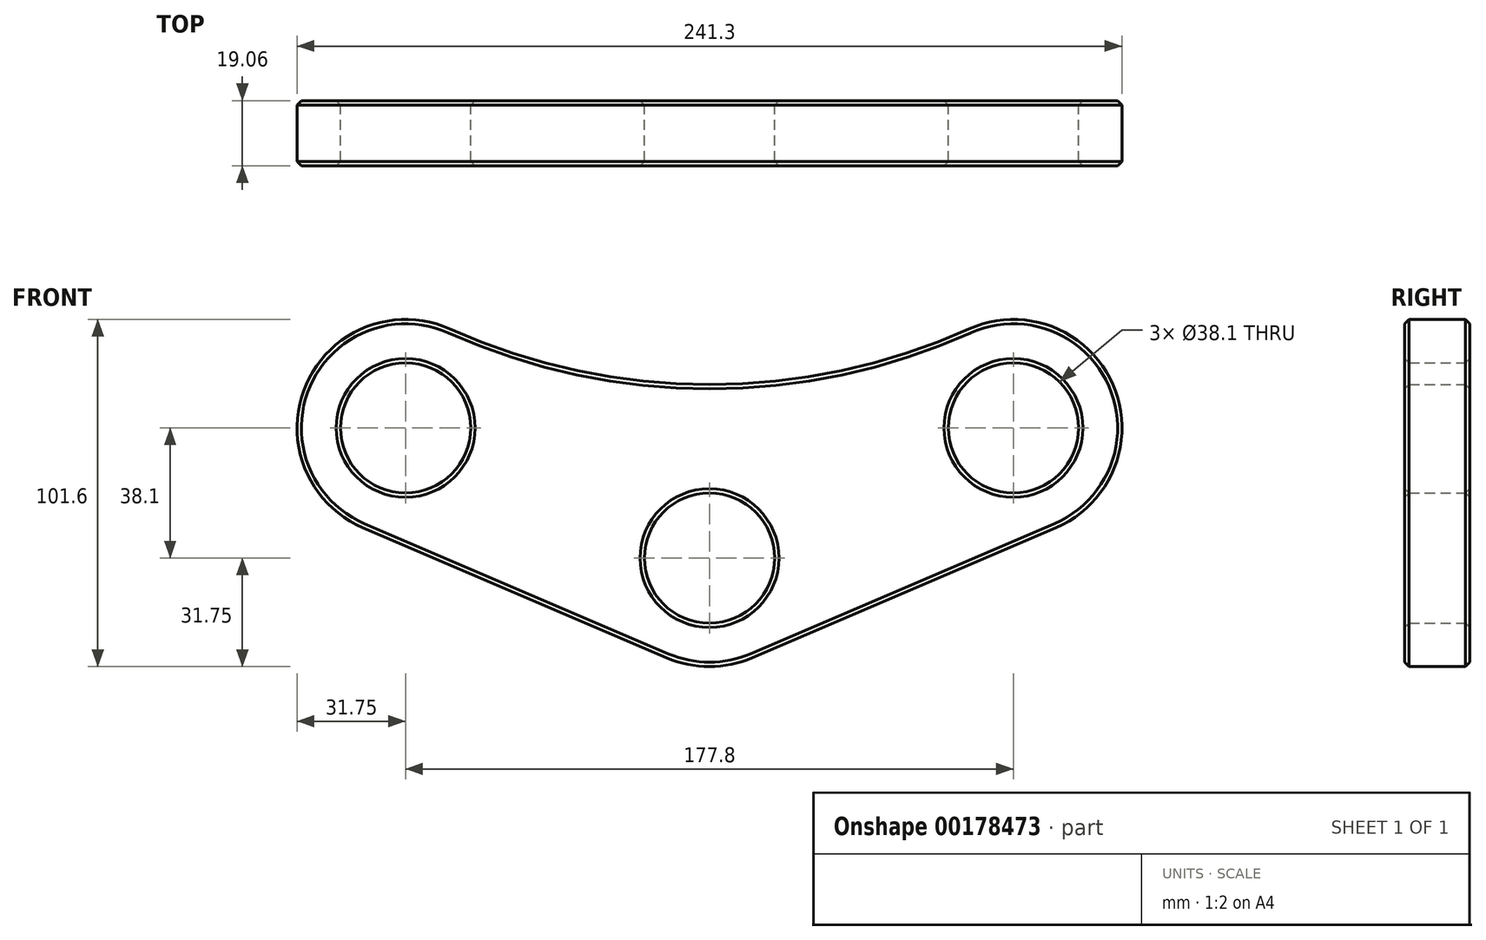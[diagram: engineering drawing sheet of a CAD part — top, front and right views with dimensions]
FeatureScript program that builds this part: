
annotation { "Feature Type Name" : "Feature", "Feature Type Description" : "" }
export const myFeature = defineFeature(function(context is Context, id is Id, definition is map)
    precondition{}
    {
        {
            var Q0;
            Q0=qCreatedBy(makeId("Front.planeOp"),FACE);
            var sketch = newSketch(context, id + "F0", { "sketchPlane" : qUnion([Q0])});
            skArc(sketch, "E0", {"start": v(-12.5, -29.18) * mm, "mid": v(0, -31.75) * mm, "end": v(12.5, -29.18) * mm});
            skArc(sketch, "E1", {"start": v(-75.9, 67.06) * mm, "mid": v(-117.97, 50.86) * mm, "end": v(-101.4, 8.92) * mm});
            skArc(sketch, "E2", {"start": v(101.4, 8.92) * mm, "mid": v(117.97, 50.86) * mm, "end": v(75.9, 67.06) * mm});
            skArc(sketch, "E3", {"start": v(-75.9, 67.06) * mm, "mid": v(0, 50.8) * mm, "end": v(75.9, 67.06) * mm});
            skPoint(sketch, "E3.first.point", {"position": v(-10.84, 113.24) * mm});
            skLineSegment(sketch, "E4", {"start": v(-101.4, 8.92) * mm, "end": v(-12.5, -29.18) * mm});
            skLineSegment(sketch, "E5", {"start": v(12.5, -29.18) * mm, "end": v(101.4, 8.92) * mm});
            skCircle(sketch, "E6", {"center": v(-88.9, 38.1) * mm, "radius": 19.05 * mm});
            skCircle(sketch, "E7", {"center": v(88.9, 38.1) * mm, "radius": 19.05 * mm});
            skCircle(sketch, "E8", {"center": v(0, 0) * mm, "radius": 19.05 * mm});
            skSolve(sketch);
        }
        {
            var Q0;
            Q0 = qSketchRegion(id + "F0", true);
            var Q1;
            Q1=makeQuery(id+"F0.imprint","IMPRINT",FACE,{"disambiguationData":[TD([[makeQuery(id+"F0.imprint","IMPRINT",EDGE,{"derivedFrom":sQuery(id+"F0.wireOp",EDGE,"2Mr1e5ev-CAVB-otBg-7zJ2-05PPhVzjL0mu")}),1.0]])]});
            extrude(context, id + "F1", {"entities" : qUnion([Q0, Q1]), "endBound" : BoundingType.SYMMETRIC, "depth" : 19.05 * mm});
        }
        {
            var Q0;
            Q0=makeQuery(id+"F1.opExtrude","CAP_EDGE",EDGE,{"disambiguationData":[OSD([sQuery(id+"F0.wireOp",EDGE,"E1")])],"isStart":false});
            var Q1;
            Q1=makeQuery(id+"F1.opExtrude","CAP_EDGE",EDGE,{"disambiguationData":[OSD([sQuery(id+"F0.wireOp",EDGE,"E4")])],"isStart":false});
            var Q2;
            Q2=makeQuery(id+"F1.opExtrude","CAP_EDGE",EDGE,{"disambiguationData":[OSD([sQuery(id+"F0.wireOp",EDGE,"E0")])],"isStart":false});
            var Q3;
            Q3=makeQuery(id+"F1.opExtrude","CAP_EDGE",EDGE,{"disambiguationData":[OSD([sQuery(id+"F0.wireOp",EDGE,"E5")])],"isStart":false});
            var Q4;
            Q4=makeQuery(id+"F1.opExtrude","CAP_EDGE",EDGE,{"disambiguationData":[OSD([sQuery(id+"F0.wireOp",EDGE,"E2")])],"isStart":false});
            var Q5;
            Q5=makeQuery(id+"F1.opExtrude","CAP_EDGE",EDGE,{"disambiguationData":[OSD([sQuery(id+"F0.wireOp",EDGE,"E3")])],"isStart":false});
            var Q6;
            Q6=makeQuery(id+"F1.opExtrude","CAP_FACE",FACE,{"disambiguationData":[OSD([sQuery(id+"F0.wireOp",EDGE,"E0"),sQuery(id+"F0.wireOp",EDGE,"E1"),sQuery(id+"F0.wireOp",EDGE,"E2"),sQuery(id+"F0.wireOp",EDGE,"E3"),sQuery(id+"F0.wireOp",EDGE,"E4"),sQuery(id+"F0.wireOp",EDGE,"E5"),sQuery(id+"F0.wireOp",EDGE,"E6"),sQuery(id+"F0.wireOp",EDGE,"E7"),sQuery(id+"F0.wireOp",EDGE,"E8")])],"isStart":true});
            var Q7;
            Q7=makeQuery(id+"F1.opExtrude","CAP_FACE",FACE,{"disambiguationData":[OSD([sQuery(id+"F0.wireOp",EDGE,"E0"),sQuery(id+"F0.wireOp",EDGE,"E1"),sQuery(id+"F0.wireOp",EDGE,"E2"),sQuery(id+"F0.wireOp",EDGE,"E3"),sQuery(id+"F0.wireOp",EDGE,"E4"),sQuery(id+"F0.wireOp",EDGE,"E5"),sQuery(id+"F0.wireOp",EDGE,"E6"),sQuery(id+"F0.wireOp",EDGE,"E7"),sQuery(id+"F0.wireOp",EDGE,"E8")])],"isStart":false});
            chamfer(context, id + "F2", {"entities" : qUnion([Q0, Q1, Q2, Q3, Q4, Q5, Q6, Q7]), "width" : 1.27 * mm, "tangentPropagation" : true});
        }
    });
